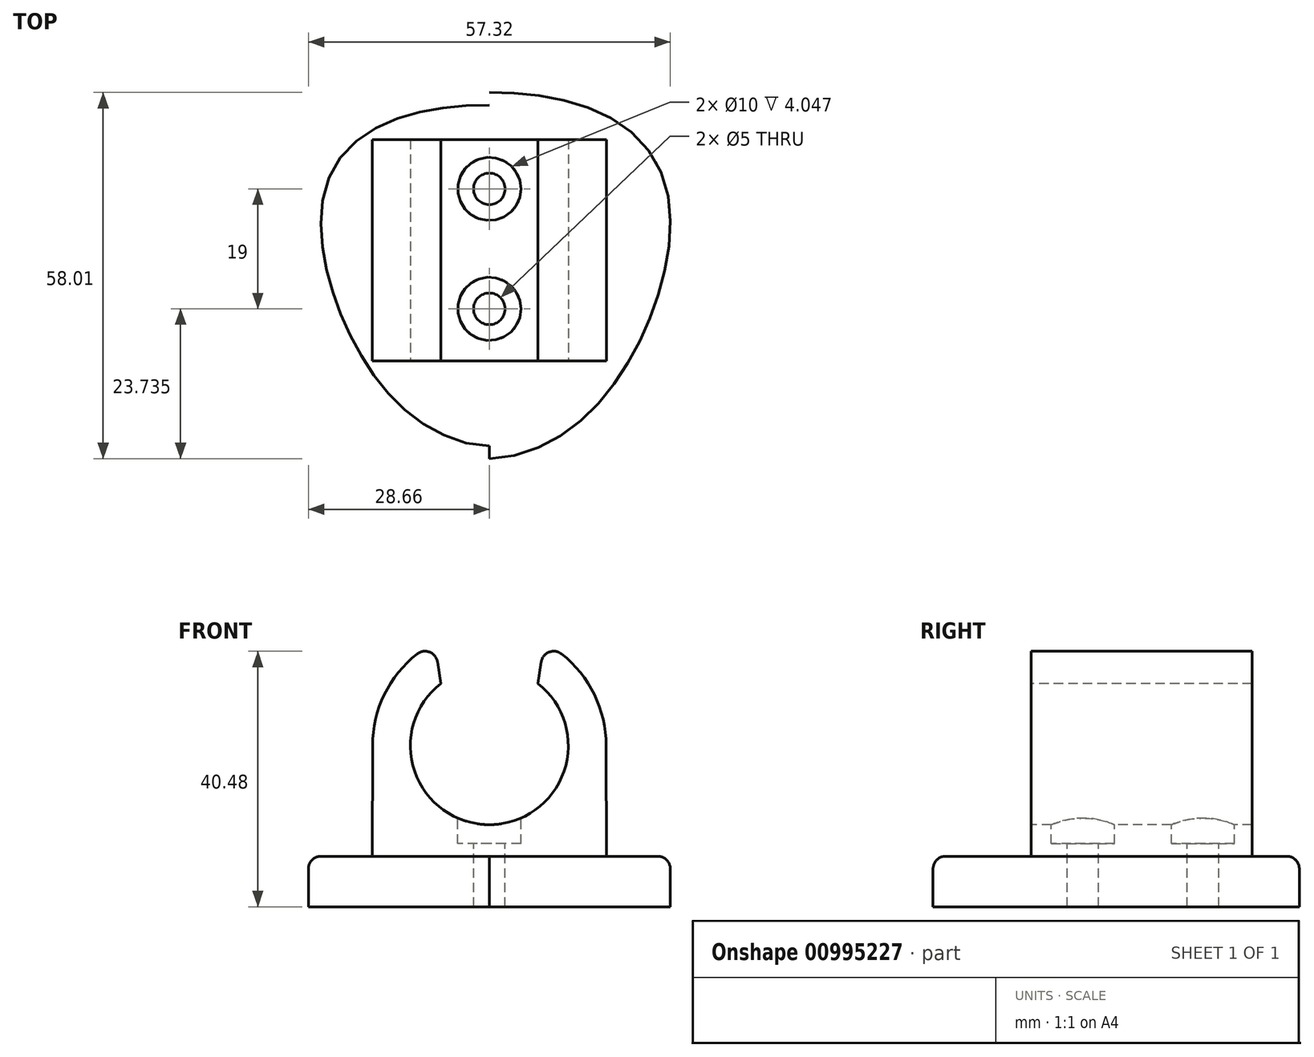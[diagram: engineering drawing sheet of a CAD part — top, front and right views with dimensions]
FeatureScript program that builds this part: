
annotation { "Feature Type Name" : "Feature", "Feature Type Description" : "" }
export const myFeature = defineFeature(function(context is Context, id is Id, definition is map)
    precondition{}
    {
        {
            var Q0;
            Q0=qCreatedBy(makeId("Top.planeOp"),FACE);
            var sketch = newSketch(context, id + "F0", { "sketchPlane" : qUnion([Q0])});
            skFitSpline(sketch, "E0", {"points": [v(0, 25) * mm, v(-28, 10) * mm, v(-16, -25.6) * mm, v(0, -33) * mm], "startDerivative": vector(-128.83, 0.56) * mm, "endDerivative": vector(40.9, 1.24) * mm});
            skFitSpline(sketch, "E1.MirrorCS", {"points": [v(0, 25) * mm, v(28, 10) * mm, v(16, -25.6) * mm, v(0, -33) * mm], "startDerivative": vector(128.83, 0.56) * mm, "endDerivative": vector(-40.9, 1.24) * mm});
            skSolve(sketch);
        }
        {
            var Q0;
            Q0 = qSketchRegion(id + "F0", true);
            extrude(context, id + "F1", {"entities" : qUnion([Q0]), "depth" : 8 * mm, "offsetDistance" : 25 * mm});
        }
        {
            var Q0;
            Q0=qCreatedBy(makeId("Front.planeOp"),FACE);
            var sketch = newSketch(context, id + "F2", { "sketchPlane" : qUnion([Q0])});
            skLineSegment(sketch, "E2", {"start": v(18.55, 8) * mm, "end": v(18.5, 25.55) * mm});
            skArc(sketch, "E3", {"start": v(18.5, 25.55) * mm, "mid": v(13.06, 38.6) * mm, "end": v(0, 44) * mm});
            skArc(sketch, "E4.MirrorCS", {"start": v(-18.5, 25.55) * mm, "mid": v(-13.06, 38.6) * mm, "end": v(0, 44) * mm});
            skLineSegment(sketch, "E5.MirrorCS", {"start": v(-18.55, 8) * mm, "end": v(-18.5, 25.55) * mm});
            skCircle(sketch, "E6", {"center": v(0, 25.5) * mm, "radius": 12.5 * mm});
            skLineSegment(sketch, "E7", {"start": v(18.55, 8) * mm, "end": v(-18.55, 8) * mm});
            skSolve(sketch);
        }
        {
            var Q0;
            Q0=makeQuery(id+"F2.imprint","IMPRINT",FACE,{"disambiguationData":[TD([[makeQuery(id+"F2.imprint","IMPRINT",EDGE,{"derivedFrom":sQuery(id+"F2.wireOp",EDGE,"E2")}),1.0]])]});
            extrude(context, id + "F3", {"entities" : qUnion([Q0]), "operationType" : NewBodyOperationType.ADD, "endBound" : BoundingType.SYMMETRIC, "oppositeDirection" : true, "depth" : 35 * mm, "offsetDistance" : 25 * mm});
        }
        {
            var Q0;
            Q0=makeQuery(id+"F3.opExtrude","CAP_FACE",FACE,{"disambiguationData":[OSD([sQuery(id+"F2.wireOp",EDGE,"E2"),sQuery(id+"F2.wireOp",EDGE,"E3"),sQuery(id+"F2.wireOp",EDGE,"E4.MirrorCS"),sQuery(id+"F2.wireOp",EDGE,"E5.MirrorCS"),sQuery(id+"F2.wireOp",EDGE,"E6"),sQuery(id+"F2.wireOp",EDGE,"E7")])],"isStart":true});
            var sketch = newSketch(context, id + "F4", { "sketchPlane" : qUnion([Q0])});
            skLineSegment(sketch, "E8", {"start": v(-7.22, 32.51) * mm, "end": v(-9, 43.81) * mm});
            skLineSegment(sketch, "E9", {"start": v(-9, 43.81) * mm, "end": v(0, 45.22) * mm});
            skLineSegment(sketch, "E10", {"start": v(-7.22, 32.51) * mm, "end": v(0, 32.51) * mm});
            skLineSegment(sketch, "E11.MirrorCS", {"start": v(9, 43.81) * mm, "end": v(0, 45.22) * mm});
            skLineSegment(sketch, "E12.MirrorCS", {"start": v(7.22, 32.51) * mm, "end": v(9, 43.81) * mm});
            skLineSegment(sketch, "E13.MirrorCS", {"start": v(7.22, 32.51) * mm, "end": v(0, 32.51) * mm});
            skSolve(sketch);
        }
        {
            var Q0;
            Q0 = qSketchRegion(id + "F4", true);
            extrude(context, id + "F5", {"entities" : qUnion([Q0]), "operationType" : NewBodyOperationType.REMOVE, "oppositeDirection" : true, "depth" : 35 * mm, "offsetDistance" : 25 * mm});
        }
        {
            var Q0;
            Q0=qCreatedBy(makeId("Top.planeOp"),FACE);
            cPlane(context, id + "F6", {"entities" : qUnion([Q0]), "cplaneType" : CPlaneType.OFFSET, "offset" : 15 * mm, "width" : 150 * mm, "height" : 150 * mm});
        }
        {
            var Q0;
            Q0=qCreatedBy(id+"F6.planeOp",FACE);
            var sketch = newSketch(context, id + "F7", { "sketchPlane" : qUnion([Q0])});
            skPoint(sketch, "E14", {"position": v(0, 9.72) * mm});
            skPoint(sketch, "E15", {"position": v(0, -9.28) * mm});
            skSolve(sketch);
        }
        {
            var Q0;
            Q0=sQuery(id+"F7.wireOp",VERTEX,"E14");
            var Q1;
            Q1=sQuery(id+"F7.wireOp",VERTEX,"E15");
            var Q2;
            Q2=makeQuery(id+"F1.opExtrude","SWEPT_BODY",BODY,{"disambiguationData":[OSD([sQuery(id+"F0.wireOp",EDGE,"E0"),sQuery(id+"F0.wireOp",EDGE,"E1.MirrorCS")])]});
            hole(context, id + "F8", {"style" : HoleStyle.C_BORE, "endStyle" : HoleEndStyle.THROUGH, "holeDiameter" : 5 * mm, "cBoreDiameter" : 10 * mm, "cBoreDepth" : 3 * mm, "majorDiameter" : 5 * mm, "isTappedThrough" : true, "tappedDepth" : 12 * mm, "tapClearance" : 3, "locations" : qUnion([Q0, Q1]), "scope" : qUnion([Q2])});
        }
        {
            var Q0;
            Q0=makeQuery(id+"F5.boolean.opBoolean","INTERSECT",EDGE,{"derivedFrom":[makeQuery(id+"F3.opExtrude","SWEPT_FACE",FACE,{"disambiguationData":[OSD([sQuery(id+"F2.wireOp",EDGE,"E3"),sQuery(id+"F2.wireOp",EDGE,"E4.MirrorCS")])]}),makeQuery(id+"F5.opExtrude","SWEPT_FACE",FACE,{"disambiguationData":[OSD([sQuery(id+"F4.wireOp",EDGE,"E8")])]})]});
            var Q1;
            Q1=makeQuery(id+"F5.boolean.opBoolean","INTERSECT",EDGE,{"derivedFrom":[makeQuery(id+"F3.opExtrude","SWEPT_FACE",FACE,{"disambiguationData":[OSD([sQuery(id+"F2.wireOp",EDGE,"E3"),sQuery(id+"F2.wireOp",EDGE,"E4.MirrorCS")])]}),makeQuery(id+"F5.opExtrude","SWEPT_FACE",FACE,{"disambiguationData":[OSD([sQuery(id+"F4.wireOp",EDGE,"E12.MirrorCS")])]})]});
            var Q2;
            Q2=makeQuery(id+"F1.opExtrude","CAP_EDGE",EDGE,{"disambiguationData":[OSD([sQuery(id+"F0.wireOp",EDGE,"E0")])],"isStart":false});
            var Q3;
            Q3=makeQuery(id+"F1.opExtrude","CAP_EDGE",EDGE,{"disambiguationData":[OSD([sQuery(id+"F0.wireOp",EDGE,"E1.MirrorCS")])],"isStart":false});
            fillet(context, id + "F9", {"entities" : qUnion([Q0, Q1, Q2, Q3]), "radius" : 2 * mm, "tangentPropagation" : true, "allowEdgeOverflow" : false});
        }
    });
